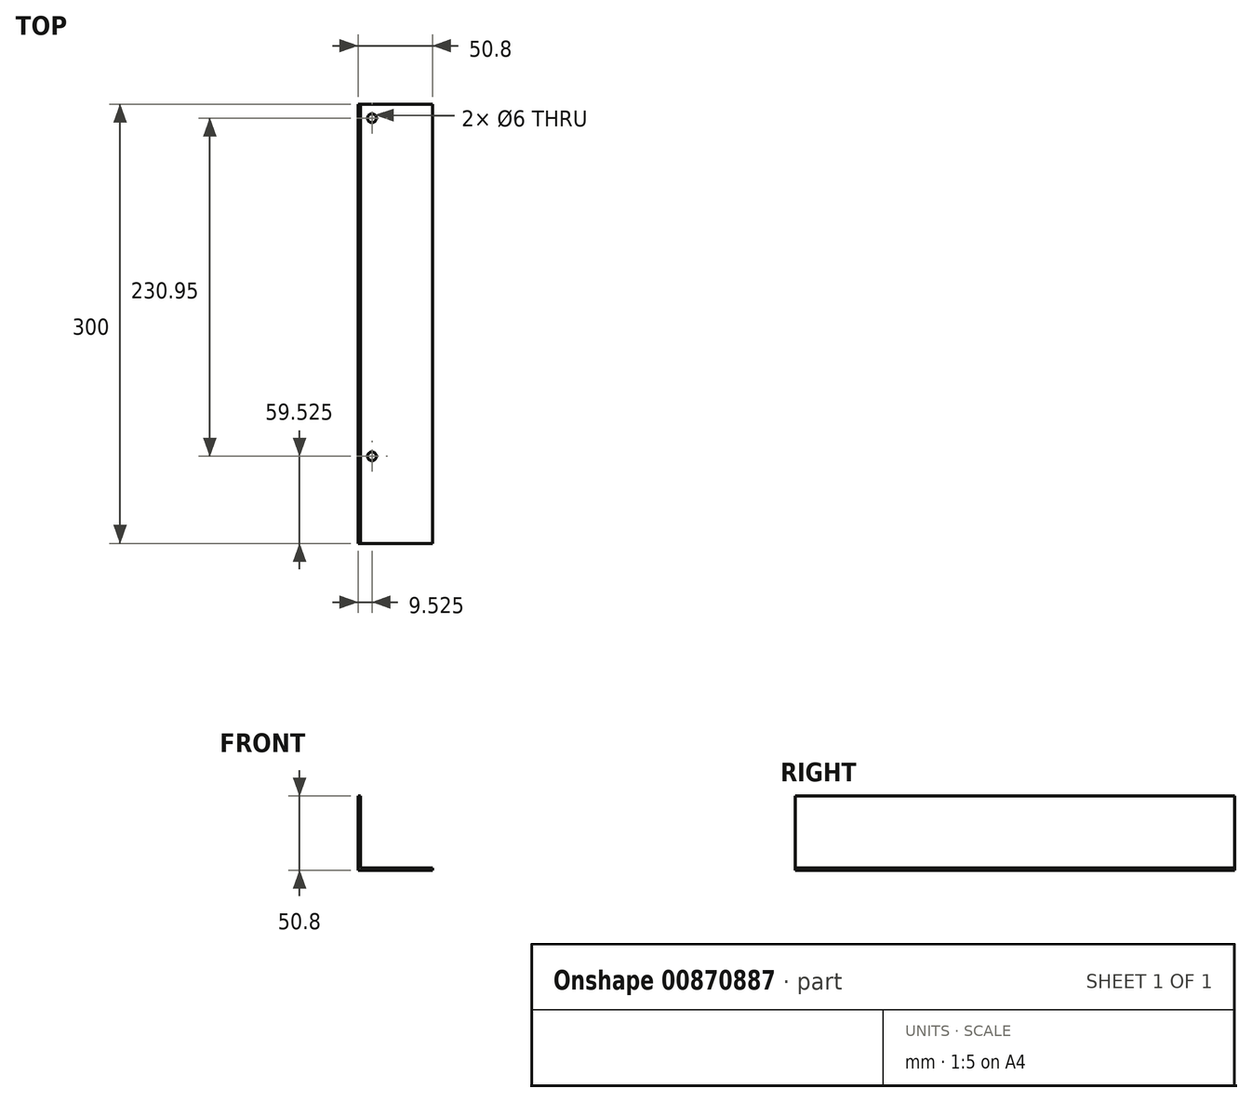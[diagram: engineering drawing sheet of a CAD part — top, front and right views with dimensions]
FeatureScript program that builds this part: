
annotation { "Feature Type Name" : "Feature", "Feature Type Description" : "" }
export const myFeature = defineFeature(function(context is Context, id is Id, definition is map)
    precondition{}
    {
        {
            var Q0;
            Q0=qCreatedBy(makeId("Front.planeOp"),FACE);
            var sketch = newSketch(context, id + "F0", { "sketchPlane" : qUnion([Q0])});
            skLineSegment(sketch, "E0", {"start": v(0, 0) * mm, "end": v(0, 50.8) * mm});
            skLineSegment(sketch, "E1", {"start": v(0, 50.8) * mm, "end": v(1.59, 50.8) * mm});
            skLineSegment(sketch, "E2", {"start": v(1.59, 50.8) * mm, "end": v(1.6, 1.59) * mm});
            skLineSegment(sketch, "E3", {"start": v(1.6, 1.59) * mm, "end": v(50.8, 1.6) * mm});
            skLineSegment(sketch, "E4", {"start": v(50.8, 1.6) * mm, "end": v(50.8, 0) * mm});
            skLineSegment(sketch, "E5", {"start": v(50.8, 0) * mm, "end": v(0, 0) * mm});
            skSolve(sketch);
        }
        {
            var Q0;
            Q0 = qSketchRegion(id + "F0", true);
            extrude(context, id + "F1", {"entities" : qUnion([Q0]), "depth" : 300 * mm, "offsetDistance" : 25 * mm});
        }
        {
            var Q0;
            Q0=qCreatedBy(makeId("Top.planeOp"),FACE);
            var sketch = newSketch(context, id + "F2", { "sketchPlane" : qUnion([Q0])});
            skPoint(sketch, "E6", {"position": v(9.52, -9.52) * mm});
            skPoint(sketch, "E7", {"position": v(9.53, -240.47) * mm});
            skCircle(sketch, "E8", {"center": v(9.52, -9.52) * mm, "radius": 3 * mm});
            skCircle(sketch, "E9", {"center": v(9.53, -240.47) * mm, "radius": 3 * mm});
            skSolve(sketch);
        }
        {
            var Q0;
            Q0 = qSketchRegion(id + "F2", true);
            extrude(context, id + "F3", {"entities" : qUnion([Q0]), "operationType" : NewBodyOperationType.REMOVE, "endBound" : BoundingType.THROUGH_ALL, "depth" : 25 * mm, "offsetDistance" : 25 * mm});
        }
    });
